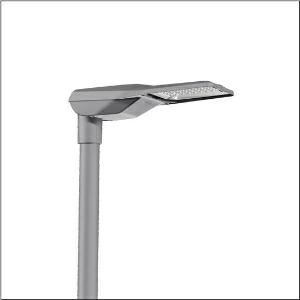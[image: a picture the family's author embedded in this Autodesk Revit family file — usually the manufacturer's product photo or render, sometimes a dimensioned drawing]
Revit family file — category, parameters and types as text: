
# Revit family: streetlight_sl_21_iq_mini___st0_8a_5xe2c41d08gb_f485
name_source: partatom
category: Lighting Fixtures
units: mm (PartAtom-declared; Revit-internal decimal feet)

## family parameters
Cut with Voids When Loaded = No
Host = Face
Light Source = No
Part Type = Normal
Room Calculation Point = No
Round Connector Dimension = Use Diameter
Shared = No

## types (1)
- --- (1 x LED, 5920 lm, 37.1 W, 4000K)
    Apparent Load = 37 VA
    CIE Flux Codes = 38 75 97 100 100
    Color Rendering = 70
    Color Temperature = 4000K
    Default Elevation = 1800 mm
    Description = Streetlight SL 21 iQ mini, mast luminaire, primary light control with lens, of PMMA, primary optical cover: cover, of toughened safety glass, transparent, light distribution: ST0.8a, light emission: direct distribution, primary light characteristic: asymmetric, installation type: post-top, side-entry, LED, High Power LED, rated luminous flux: 5.920lm, luminous efficacy: 160lm/W, light colour: 740, colour temperature: 4000K, control gear: iQ-Comfort, control: Auto-Match, Temp-Guard, Lumen-Switch, Night-Set, Smart-Wire, Light-Fading, Desk-Remote (wireless, voltage-free reading and setting of iQ features in the workshop via application-optimized NFC function/RFID function), optimised constant luminous flux control (CLO 2.0), pre-setting: linear dimming characteristic, mains connection: 220..240V, AC, 50/60Hz, start of lifetime: 37W, end of service life: 39W, reduction: 18W, luminaire housing, of diecast aluminium, powder-coated, SITECO metallic grey (DB 702S), corrosivity category C5 high according to DIN EN ISO 12944, please order mast flange separately, inclination adjustable: 0°, 5°, 10°, 15°, sealing non-destructively replaceable, multi-level sealing system, length: 628mm, width: 235mm, height: 110mm, mast flange for spigot size: 42mm (side-entry): 5XC10008XM4, 60/48mm (side-entry/post-top): 5XC10108XM2, 76/60mm (side-entry/post-top): 5XC10108XM1, mounting height: 4..8m, protection rating (complete): IP66, insulation class (complete): insulation class II (safety insulation), certification: CE, ENEC, ENEC+, VDE, impact resistance: IK10, permissible operating ambient temperature for outdoor applications: -40..+50°C, standard-compliant lighting for roads and squares, packaging unit: 1 piece

Light Distribution: ST0.8a
    Height = 110 mm
    Lamp = 1 x LED
    Lamp Light Flux = 5920 lm
    Lamp Power = 37.1 W
    Lamp count = 1
    Length = 625 mm
    Luminous efficacy = 160 lm/W
    Manufacturer = Siteco
    ModVariant = No
    Model = 5XE2C41D08GB
    Mounting Place = Pole
    Mounting Type = Pole top
    Number of Poles = 1
    OnlyDefault = Yes
    Power Factor = 1
    Product Name = Streetlight SL 21 iQ mini | ST0.8a
    Product group = mast luminaire | pylon top
    ProductGroupID = 6100
    Protection Class = Protection class II
    Protection Degree = IP 66
    RLX_Detail_Level = 1
    RLX_Emergency_Light_Flux = 0 lm
    RLX_Emergency_Type = 0
    RLX_Emergency_Type_DB = No
    RlxData = <blob elided: 26369 chars, md5=3fb0e3e5>
    Socket = socket
    Standby Power = 0 W
    System Light Flux = 5920 lm
    System Power = 37 W
    Type Comments = factory setting: luminous flux: 100 % | dim-lin: 254 | 385 mA
    Type Image = l_1003519.jpg
    URL = http://relux.com
    VarID = @adj_184661
    Voltage = 0 V
    Weight = 0.00 kg
    Width = 234 mm

## geometry (parser evidence)
native form markers: Blend x4, Sweep x11
no freeform markers — native parametric forms only
